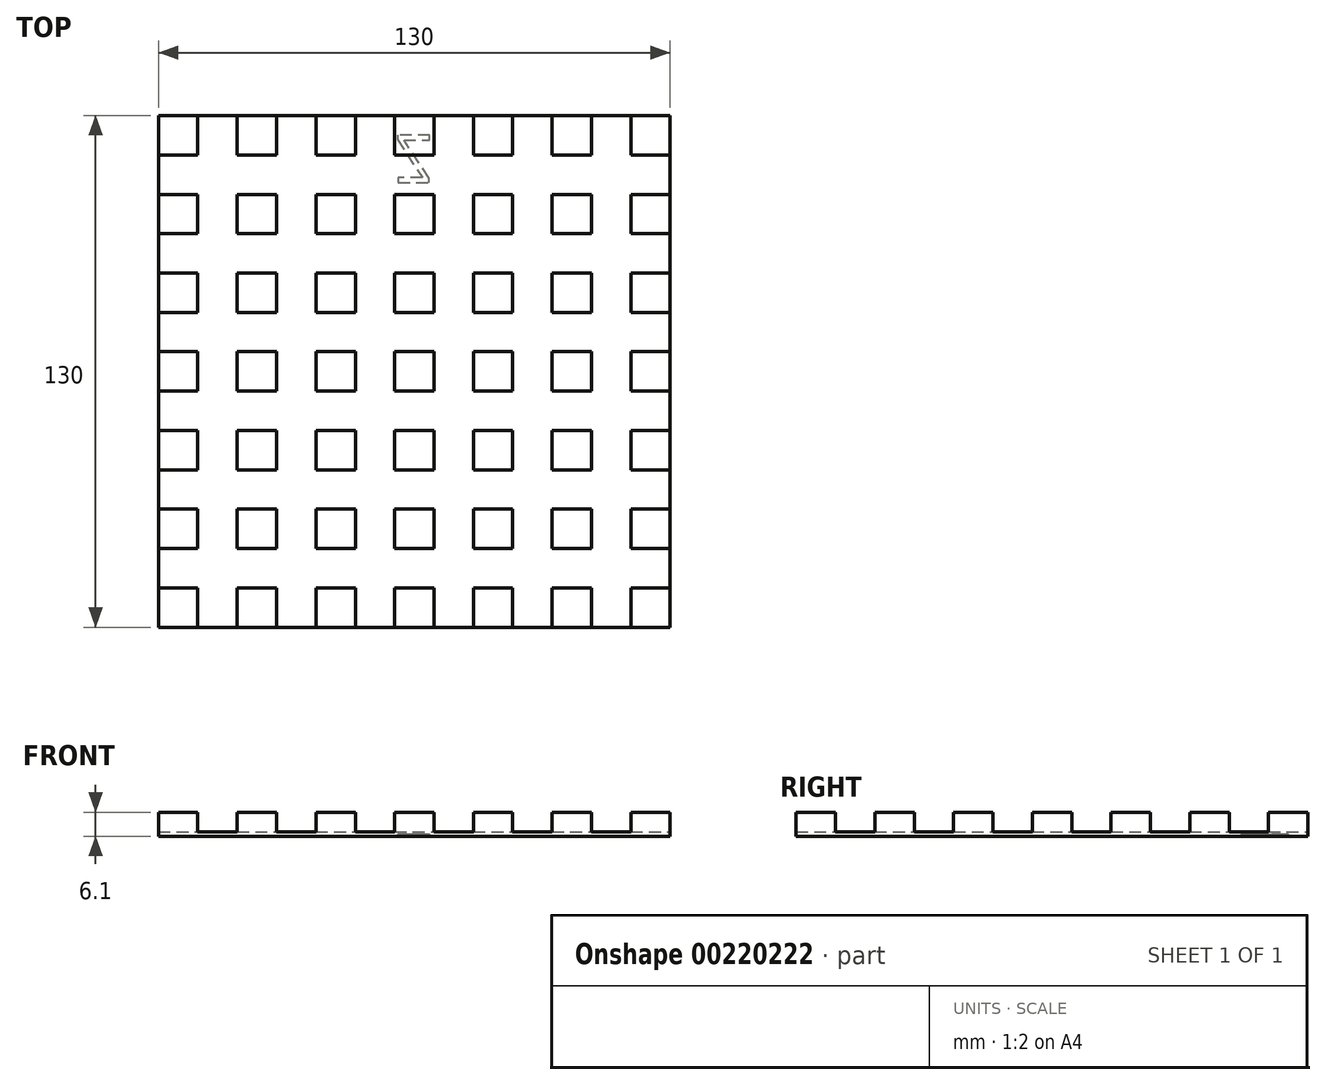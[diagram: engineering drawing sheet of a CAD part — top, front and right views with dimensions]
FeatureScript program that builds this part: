
annotation { "Feature Type Name" : "Feature", "Feature Type Description" : "" }
export const myFeature = defineFeature(function(context is Context, id is Id, definition is map)
    precondition{}
    {
        {
            var Q0;
            Q0=qCreatedBy(makeId("Top.planeOp"),FACE);
            var sketch = newSketch(context, id + "F0", { "sketchPlane" : qUnion([Q0])});
            skLineSegment(sketch, "E0.bottom", {"start": v(0, 0) * mm, "end": v(130, 0) * mm});
            skLineSegment(sketch, "E0.top", {"start": v(0, 130) * mm, "end": v(130, 130) * mm});
            skLineSegment(sketch, "E0.left", {"start": v(0, 0) * mm, "end": v(0, 130) * mm});
            skLineSegment(sketch, "E0.right", {"start": v(130, 0) * mm, "end": v(130, 130) * mm});
            skSolve(sketch);
        }
        {
            var Q0;
            Q0 = qSketchRegion(id + "F0", true);
            extrude(context, id + "F1", {"entities" : qUnion([Q0]), "depth" : 1.1 * mm});
        }
        {
            var Q0;
            Q0=makeQuery(id+"F1.opExtrude","CAP_FACE",FACE,{"disambiguationData":[OSD([sQuery(id+"F0.wireOp",EDGE,"E0.bottom"),sQuery(id+"F0.wireOp",EDGE,"E0.top"),sQuery(id+"F0.wireOp",EDGE,"E0.left"),sQuery(id+"F0.wireOp",EDGE,"E0.right")])],"isStart":false});
            var sketch = newSketch(context, id + "F2", { "sketchPlane" : qUnion([Q0])});
            skLineSegment(sketch, "E1", {"start": v(0, 0) * mm, "end": v(130, 130) * mm, "construction": true});
            skLineSegment(sketch, "E2.bottom", {"start": v(0, 0) * mm, "end": v(130, 0) * mm, "construction": true});
            skLineSegment(sketch, "E2.top", {"start": v(0, 130) * mm, "end": v(130, 130) * mm, "construction": true});
            skLineSegment(sketch, "E2.left", {"start": v(0, 0) * mm, "end": v(0, 130) * mm, "construction": true});
            skLineSegment(sketch, "E2.right", {"start": v(130, 0) * mm, "end": v(130, 130) * mm, "construction": true});
            skPoint(sketch, "E2.middle", {"position": v(65, 65) * mm});
            skLineSegment(sketch, "E3.bottom", {"start": v(0, 0) * mm, "end": v(10, 0) * mm});
            skLineSegment(sketch, "E3.top", {"start": v(0, 10) * mm, "end": v(10, 10) * mm});
            skLineSegment(sketch, "E3.left", {"start": v(0, 0) * mm, "end": v(0, 10) * mm});
            skLineSegment(sketch, "E3.right", {"start": v(10, 0) * mm, "end": v(10, 10) * mm});
            skLineSegment(sketch, "E4.0.1.0", {"start": v(10, 20) * mm, "end": v(10, 30) * mm});
            skLineSegment(sketch, "E4.0.1.1", {"start": v(0, 20) * mm, "end": v(0, 30) * mm});
            skLineSegment(sketch, "E4.0.1.2", {"start": v(0, 20) * mm, "end": v(10, 20) * mm});
            skLineSegment(sketch, "E4.0.1.3", {"start": v(0, 30) * mm, "end": v(10, 30) * mm});
            skLineSegment(sketch, "E4.0.2.0", {"start": v(10, 40) * mm, "end": v(10, 50) * mm});
            skLineSegment(sketch, "E4.0.2.1", {"start": v(0, 40) * mm, "end": v(0, 50) * mm});
            skLineSegment(sketch, "E4.0.2.2", {"start": v(0, 40) * mm, "end": v(10, 40) * mm});
            skLineSegment(sketch, "E4.0.2.3", {"start": v(0, 50) * mm, "end": v(10, 50) * mm});
            skLineSegment(sketch, "E4.0.3.0", {"start": v(10, 60) * mm, "end": v(10, 70) * mm});
            skLineSegment(sketch, "E4.0.3.1", {"start": v(0, 60) * mm, "end": v(0, 70) * mm});
            skLineSegment(sketch, "E4.0.3.2", {"start": v(0, 60) * mm, "end": v(10, 60) * mm});
            skLineSegment(sketch, "E4.0.3.3", {"start": v(0, 70) * mm, "end": v(10, 70) * mm});
            skLineSegment(sketch, "E4.0.4.0", {"start": v(10, 80) * mm, "end": v(10, 90) * mm});
            skLineSegment(sketch, "E4.0.4.1", {"start": v(0, 80) * mm, "end": v(0, 90) * mm});
            skLineSegment(sketch, "E4.0.4.2", {"start": v(0, 80) * mm, "end": v(10, 80) * mm});
            skLineSegment(sketch, "E4.0.4.3", {"start": v(0, 90) * mm, "end": v(10, 90) * mm});
            skLineSegment(sketch, "E4.0.5.0", {"start": v(10, 100) * mm, "end": v(10, 110) * mm});
            skLineSegment(sketch, "E4.0.5.1", {"start": v(0, 100) * mm, "end": v(0, 110) * mm});
            skLineSegment(sketch, "E4.0.5.2", {"start": v(0, 100) * mm, "end": v(10, 100) * mm});
            skLineSegment(sketch, "E4.0.5.3", {"start": v(0, 110) * mm, "end": v(10, 110) * mm});
            skLineSegment(sketch, "E4.1.0.0", {"start": v(30, 0) * mm, "end": v(30, 10) * mm});
            skLineSegment(sketch, "E4.1.0.1", {"start": v(20, 0) * mm, "end": v(20, 10) * mm});
            skLineSegment(sketch, "E4.1.0.2", {"start": v(20, 0) * mm, "end": v(30, 0) * mm});
            skLineSegment(sketch, "E4.1.0.3", {"start": v(20, 10) * mm, "end": v(30, 10) * mm});
            skLineSegment(sketch, "E4.1.1.0", {"start": v(30, 20) * mm, "end": v(30, 30) * mm});
            skLineSegment(sketch, "E4.1.1.1", {"start": v(20, 20) * mm, "end": v(20, 30) * mm});
            skLineSegment(sketch, "E4.1.1.2", {"start": v(20, 20) * mm, "end": v(30, 20) * mm});
            skLineSegment(sketch, "E4.1.1.3", {"start": v(20, 30) * mm, "end": v(30, 30) * mm});
            skLineSegment(sketch, "E4.1.2.0", {"start": v(30, 40) * mm, "end": v(30, 50) * mm});
            skLineSegment(sketch, "E4.1.2.1", {"start": v(20, 40) * mm, "end": v(20, 50) * mm});
            skLineSegment(sketch, "E4.1.2.2", {"start": v(20, 40) * mm, "end": v(30, 40) * mm});
            skLineSegment(sketch, "E4.1.2.3", {"start": v(20, 50) * mm, "end": v(30, 50) * mm});
            skLineSegment(sketch, "E4.1.3.0", {"start": v(30, 60) * mm, "end": v(30, 70) * mm});
            skLineSegment(sketch, "E4.1.3.1", {"start": v(20, 60) * mm, "end": v(20, 70) * mm});
            skLineSegment(sketch, "E4.1.3.2", {"start": v(20, 60) * mm, "end": v(30, 60) * mm});
            skLineSegment(sketch, "E4.1.3.3", {"start": v(20, 70) * mm, "end": v(30, 70) * mm});
            skLineSegment(sketch, "E4.1.4.0", {"start": v(30, 80) * mm, "end": v(30, 90) * mm});
            skLineSegment(sketch, "E4.1.4.1", {"start": v(20, 80) * mm, "end": v(20, 90) * mm});
            skLineSegment(sketch, "E4.1.4.2", {"start": v(20, 80) * mm, "end": v(30, 80) * mm});
            skLineSegment(sketch, "E4.1.4.3", {"start": v(20, 90) * mm, "end": v(30, 90) * mm});
            skLineSegment(sketch, "E4.1.5.0", {"start": v(30, 100) * mm, "end": v(30, 110) * mm});
            skLineSegment(sketch, "E4.1.5.1", {"start": v(20, 100) * mm, "end": v(20, 110) * mm});
            skLineSegment(sketch, "E4.1.5.2", {"start": v(20, 100) * mm, "end": v(30, 100) * mm});
            skLineSegment(sketch, "E4.1.5.3", {"start": v(20, 110) * mm, "end": v(30, 110) * mm});
            skLineSegment(sketch, "E4.2.0.0", {"start": v(50, 0) * mm, "end": v(50, 10) * mm});
            skLineSegment(sketch, "E4.2.0.1", {"start": v(40, 0) * mm, "end": v(40, 10) * mm});
            skLineSegment(sketch, "E4.2.0.2", {"start": v(40, 0) * mm, "end": v(50, 0) * mm});
            skLineSegment(sketch, "E4.2.0.3", {"start": v(40, 10) * mm, "end": v(50, 10) * mm});
            skLineSegment(sketch, "E4.2.1.0", {"start": v(50, 20) * mm, "end": v(50, 30) * mm});
            skLineSegment(sketch, "E4.2.1.1", {"start": v(40, 20) * mm, "end": v(40, 30) * mm});
            skLineSegment(sketch, "E4.2.1.2", {"start": v(40, 20) * mm, "end": v(50, 20) * mm});
            skLineSegment(sketch, "E4.2.1.3", {"start": v(40, 30) * mm, "end": v(50, 30) * mm});
            skLineSegment(sketch, "E4.2.2.0", {"start": v(50, 40) * mm, "end": v(50, 50) * mm});
            skLineSegment(sketch, "E4.2.2.1", {"start": v(40, 40) * mm, "end": v(40, 50) * mm});
            skLineSegment(sketch, "E4.2.2.2", {"start": v(40, 40) * mm, "end": v(50, 40) * mm});
            skLineSegment(sketch, "E4.2.2.3", {"start": v(40, 50) * mm, "end": v(50, 50) * mm});
            skLineSegment(sketch, "E4.2.3.0", {"start": v(50, 60) * mm, "end": v(50, 70) * mm});
            skLineSegment(sketch, "E4.2.3.1", {"start": v(40, 60) * mm, "end": v(40, 70) * mm});
            skLineSegment(sketch, "E4.2.3.2", {"start": v(40, 60) * mm, "end": v(50, 60) * mm});
            skLineSegment(sketch, "E4.2.3.3", {"start": v(40, 70) * mm, "end": v(50, 70) * mm});
            skLineSegment(sketch, "E4.2.4.0", {"start": v(50, 80) * mm, "end": v(50, 90) * mm});
            skLineSegment(sketch, "E4.2.4.1", {"start": v(40, 80) * mm, "end": v(40, 90) * mm});
            skLineSegment(sketch, "E4.2.4.2", {"start": v(40, 80) * mm, "end": v(50, 80) * mm});
            skLineSegment(sketch, "E4.2.4.3", {"start": v(40, 90) * mm, "end": v(50, 90) * mm});
            skLineSegment(sketch, "E4.2.5.0", {"start": v(50, 100) * mm, "end": v(50, 110) * mm});
            skLineSegment(sketch, "E4.2.5.1", {"start": v(40, 100) * mm, "end": v(40, 110) * mm});
            skLineSegment(sketch, "E4.2.5.2", {"start": v(40, 100) * mm, "end": v(50, 100) * mm});
            skLineSegment(sketch, "E4.2.5.3", {"start": v(40, 110) * mm, "end": v(50, 110) * mm});
            skLineSegment(sketch, "E4.3.0.0", {"start": v(70, 0) * mm, "end": v(70, 10) * mm});
            skLineSegment(sketch, "E4.3.0.1", {"start": v(60, 0) * mm, "end": v(60, 10) * mm});
            skLineSegment(sketch, "E4.3.0.2", {"start": v(60, 0) * mm, "end": v(70, 0) * mm});
            skLineSegment(sketch, "E4.3.0.3", {"start": v(60, 10) * mm, "end": v(70, 10) * mm});
            skLineSegment(sketch, "E4.3.1.0", {"start": v(70, 20) * mm, "end": v(70, 30) * mm});
            skLineSegment(sketch, "E4.3.1.1", {"start": v(60, 20) * mm, "end": v(60, 30) * mm});
            skLineSegment(sketch, "E4.3.1.2", {"start": v(60, 20) * mm, "end": v(70, 20) * mm});
            skLineSegment(sketch, "E4.3.1.3", {"start": v(60, 30) * mm, "end": v(70, 30) * mm});
            skLineSegment(sketch, "E4.3.2.0", {"start": v(70, 40) * mm, "end": v(70, 50) * mm});
            skLineSegment(sketch, "E4.3.2.1", {"start": v(60, 40) * mm, "end": v(60, 50) * mm});
            skLineSegment(sketch, "E4.3.2.2", {"start": v(60, 40) * mm, "end": v(70, 40) * mm});
            skLineSegment(sketch, "E4.3.2.3", {"start": v(60, 50) * mm, "end": v(70, 50) * mm});
            skLineSegment(sketch, "E4.3.3.0", {"start": v(70, 60) * mm, "end": v(70, 70) * mm});
            skLineSegment(sketch, "E4.3.3.1", {"start": v(60, 60) * mm, "end": v(60, 70) * mm});
            skLineSegment(sketch, "E4.3.3.2", {"start": v(60, 60) * mm, "end": v(70, 60) * mm});
            skLineSegment(sketch, "E4.3.3.3", {"start": v(60, 70) * mm, "end": v(70, 70) * mm});
            skLineSegment(sketch, "E4.3.4.0", {"start": v(70, 80) * mm, "end": v(70, 90) * mm});
            skLineSegment(sketch, "E4.3.4.1", {"start": v(60, 80) * mm, "end": v(60, 90) * mm});
            skLineSegment(sketch, "E4.3.4.2", {"start": v(60, 80) * mm, "end": v(70, 80) * mm});
            skLineSegment(sketch, "E4.3.4.3", {"start": v(60, 90) * mm, "end": v(70, 90) * mm});
            skLineSegment(sketch, "E4.3.5.0", {"start": v(70, 100) * mm, "end": v(70, 110) * mm});
            skLineSegment(sketch, "E4.3.5.1", {"start": v(60, 100) * mm, "end": v(60, 110) * mm});
            skLineSegment(sketch, "E4.3.5.2", {"start": v(60, 100) * mm, "end": v(70, 100) * mm});
            skLineSegment(sketch, "E4.3.5.3", {"start": v(60, 110) * mm, "end": v(70, 110) * mm});
            skLineSegment(sketch, "E4.4.0.0", {"start": v(90, 0) * mm, "end": v(90, 10) * mm});
            skLineSegment(sketch, "E4.4.0.1", {"start": v(80, 0) * mm, "end": v(80, 10) * mm});
            skLineSegment(sketch, "E4.4.0.2", {"start": v(80, 0) * mm, "end": v(90, 0) * mm});
            skLineSegment(sketch, "E4.4.0.3", {"start": v(80, 10) * mm, "end": v(90, 10) * mm});
            skLineSegment(sketch, "E4.4.1.0", {"start": v(90, 20) * mm, "end": v(90, 30) * mm});
            skLineSegment(sketch, "E4.4.1.1", {"start": v(80, 20) * mm, "end": v(80, 30) * mm});
            skLineSegment(sketch, "E4.4.1.2", {"start": v(80, 20) * mm, "end": v(90, 20) * mm});
            skLineSegment(sketch, "E4.4.1.3", {"start": v(80, 30) * mm, "end": v(90, 30) * mm});
            skLineSegment(sketch, "E4.4.2.0", {"start": v(90, 40) * mm, "end": v(90, 50) * mm});
            skLineSegment(sketch, "E4.4.2.1", {"start": v(80, 40) * mm, "end": v(80, 50) * mm});
            skLineSegment(sketch, "E4.4.2.2", {"start": v(80, 40) * mm, "end": v(90, 40) * mm});
            skLineSegment(sketch, "E4.4.2.3", {"start": v(80, 50) * mm, "end": v(90, 50) * mm});
            skLineSegment(sketch, "E4.4.3.0", {"start": v(90, 60) * mm, "end": v(90, 70) * mm});
            skLineSegment(sketch, "E4.4.3.1", {"start": v(80, 60) * mm, "end": v(80, 70) * mm});
            skLineSegment(sketch, "E4.4.3.2", {"start": v(80, 60) * mm, "end": v(90, 60) * mm});
            skLineSegment(sketch, "E4.4.3.3", {"start": v(80, 70) * mm, "end": v(90, 70) * mm});
            skLineSegment(sketch, "E4.4.4.0", {"start": v(90, 80) * mm, "end": v(90, 90) * mm});
            skLineSegment(sketch, "E4.4.4.1", {"start": v(80, 80) * mm, "end": v(80, 90) * mm});
            skLineSegment(sketch, "E4.4.4.2", {"start": v(80, 80) * mm, "end": v(90, 80) * mm});
            skLineSegment(sketch, "E4.4.4.3", {"start": v(80, 90) * mm, "end": v(90, 90) * mm});
            skLineSegment(sketch, "E4.4.5.0", {"start": v(90, 100) * mm, "end": v(90, 110) * mm});
            skLineSegment(sketch, "E4.4.5.1", {"start": v(80, 100) * mm, "end": v(80, 110) * mm});
            skLineSegment(sketch, "E4.4.5.2", {"start": v(80, 100) * mm, "end": v(90, 100) * mm});
            skLineSegment(sketch, "E4.4.5.3", {"start": v(80, 110) * mm, "end": v(90, 110) * mm});
            skLineSegment(sketch, "E4.5.0.0", {"start": v(110, 0) * mm, "end": v(110, 10) * mm});
            skLineSegment(sketch, "E4.5.0.1", {"start": v(100, 0) * mm, "end": v(100, 10) * mm});
            skLineSegment(sketch, "E4.5.0.2", {"start": v(100, 0) * mm, "end": v(110, 0) * mm});
            skLineSegment(sketch, "E4.5.0.3", {"start": v(100, 10) * mm, "end": v(110, 10) * mm});
            skLineSegment(sketch, "E4.5.1.0", {"start": v(110, 20) * mm, "end": v(110, 30) * mm});
            skLineSegment(sketch, "E4.5.1.1", {"start": v(100, 20) * mm, "end": v(100, 30) * mm});
            skLineSegment(sketch, "E4.5.1.2", {"start": v(100, 20) * mm, "end": v(110, 20) * mm});
            skLineSegment(sketch, "E4.5.1.3", {"start": v(100, 30) * mm, "end": v(110, 30) * mm});
            skLineSegment(sketch, "E4.5.2.0", {"start": v(110, 40) * mm, "end": v(110, 50) * mm});
            skLineSegment(sketch, "E4.5.2.1", {"start": v(100, 40) * mm, "end": v(100, 50) * mm});
            skLineSegment(sketch, "E4.5.2.2", {"start": v(100, 40) * mm, "end": v(110, 40) * mm});
            skLineSegment(sketch, "E4.5.2.3", {"start": v(100, 50) * mm, "end": v(110, 50) * mm});
            skLineSegment(sketch, "E4.5.3.0", {"start": v(110, 60) * mm, "end": v(110, 70) * mm});
            skLineSegment(sketch, "E4.5.3.1", {"start": v(100, 60) * mm, "end": v(100, 70) * mm});
            skLineSegment(sketch, "E4.5.3.2", {"start": v(100, 60) * mm, "end": v(110, 60) * mm});
            skLineSegment(sketch, "E4.5.3.3", {"start": v(100, 70) * mm, "end": v(110, 70) * mm});
            skLineSegment(sketch, "E4.5.4.0", {"start": v(110, 80) * mm, "end": v(110, 90) * mm});
            skLineSegment(sketch, "E4.5.4.1", {"start": v(100, 80) * mm, "end": v(100, 90) * mm});
            skLineSegment(sketch, "E4.5.4.2", {"start": v(100, 80) * mm, "end": v(110, 80) * mm});
            skLineSegment(sketch, "E4.5.4.3", {"start": v(100, 90) * mm, "end": v(110, 90) * mm});
            skLineSegment(sketch, "E4.5.5.0", {"start": v(110, 100) * mm, "end": v(110, 110) * mm});
            skLineSegment(sketch, "E4.5.5.1", {"start": v(100, 100) * mm, "end": v(100, 110) * mm});
            skLineSegment(sketch, "E4.5.5.2", {"start": v(100, 100) * mm, "end": v(110, 100) * mm});
            skLineSegment(sketch, "E4.5.5.3", {"start": v(100, 110) * mm, "end": v(110, 110) * mm});
            skLineSegment(sketch, "E4.direction1", {"start": v(0, 0) * mm, "end": v(20, 0) * mm, "construction": true});
            skLineSegment(sketch, "E4.direction2", {"start": v(0, 0) * mm, "end": v(0, 20) * mm, "construction": true});
            skLineSegment(sketch, "E5.0.0.6", {"start": v(10, 120) * mm, "end": v(10, 130) * mm});
            skLineSegment(sketch, "E5.3.0.6", {"start": v(0, 120) * mm, "end": v(0, 130) * mm});
            skLineSegment(sketch, "E5.6.0.6", {"start": v(0, 120) * mm, "end": v(10, 120) * mm});
            skLineSegment(sketch, "E5.9.0.6", {"start": v(0, 130) * mm, "end": v(10, 130) * mm});
            skLineSegment(sketch, "E5.0.1.6", {"start": v(30, 120) * mm, "end": v(30, 130) * mm});
            skLineSegment(sketch, "E5.3.1.6", {"start": v(20, 120) * mm, "end": v(20, 130) * mm});
            skLineSegment(sketch, "E5.6.1.6", {"start": v(20, 120) * mm, "end": v(30, 120) * mm});
            skLineSegment(sketch, "E5.9.1.6", {"start": v(20, 130) * mm, "end": v(30, 130) * mm});
            skLineSegment(sketch, "E5.0.2.6", {"start": v(50, 120) * mm, "end": v(50, 130) * mm});
            skLineSegment(sketch, "E5.3.2.6", {"start": v(40, 120) * mm, "end": v(40, 130) * mm});
            skLineSegment(sketch, "E5.6.2.6", {"start": v(40, 120) * mm, "end": v(50, 120) * mm});
            skLineSegment(sketch, "E5.9.2.6", {"start": v(40, 130) * mm, "end": v(50, 130) * mm});
            skLineSegment(sketch, "E5.0.3.6", {"start": v(70, 120) * mm, "end": v(70, 130) * mm});
            skLineSegment(sketch, "E5.3.3.6", {"start": v(60, 120) * mm, "end": v(60, 130) * mm});
            skLineSegment(sketch, "E5.6.3.6", {"start": v(60, 120) * mm, "end": v(70, 120) * mm});
            skLineSegment(sketch, "E5.9.3.6", {"start": v(60, 130) * mm, "end": v(70, 130) * mm});
            skLineSegment(sketch, "E5.0.4.6", {"start": v(90, 120) * mm, "end": v(90, 130) * mm});
            skLineSegment(sketch, "E5.3.4.6", {"start": v(80, 120) * mm, "end": v(80, 130) * mm});
            skLineSegment(sketch, "E5.6.4.6", {"start": v(80, 120) * mm, "end": v(90, 120) * mm});
            skLineSegment(sketch, "E5.9.4.6", {"start": v(80, 130) * mm, "end": v(90, 130) * mm});
            skLineSegment(sketch, "E5.0.5.6", {"start": v(110, 120) * mm, "end": v(110, 130) * mm});
            skLineSegment(sketch, "E5.3.5.6", {"start": v(100, 120) * mm, "end": v(100, 130) * mm});
            skLineSegment(sketch, "E5.6.5.6", {"start": v(100, 120) * mm, "end": v(110, 120) * mm});
            skLineSegment(sketch, "E5.9.5.6", {"start": v(100, 130) * mm, "end": v(110, 130) * mm});
            skLineSegment(sketch, "E6.0.6.0", {"start": v(130, 0) * mm, "end": v(130, 10) * mm});
            skLineSegment(sketch, "E6.3.6.0", {"start": v(120, 0) * mm, "end": v(120, 10) * mm});
            skLineSegment(sketch, "E6.6.6.0", {"start": v(120, 0) * mm, "end": v(130, 0) * mm});
            skLineSegment(sketch, "E6.9.6.0", {"start": v(120, 10) * mm, "end": v(130, 10) * mm});
            skLineSegment(sketch, "E6.0.6.1", {"start": v(130, 20) * mm, "end": v(130, 30) * mm});
            skLineSegment(sketch, "E6.3.6.1", {"start": v(120, 20) * mm, "end": v(120, 30) * mm});
            skLineSegment(sketch, "E6.6.6.1", {"start": v(120, 20) * mm, "end": v(130, 20) * mm});
            skLineSegment(sketch, "E6.9.6.1", {"start": v(120, 30) * mm, "end": v(130, 30) * mm});
            skLineSegment(sketch, "E6.0.6.2", {"start": v(130, 40) * mm, "end": v(130, 50) * mm});
            skLineSegment(sketch, "E6.3.6.2", {"start": v(120, 40) * mm, "end": v(120, 50) * mm});
            skLineSegment(sketch, "E6.6.6.2", {"start": v(120, 40) * mm, "end": v(130, 40) * mm});
            skLineSegment(sketch, "E6.9.6.2", {"start": v(120, 50) * mm, "end": v(130, 50) * mm});
            skLineSegment(sketch, "E6.0.6.3", {"start": v(130, 60) * mm, "end": v(130, 70) * mm});
            skLineSegment(sketch, "E6.3.6.3", {"start": v(120, 60) * mm, "end": v(120, 70) * mm});
            skLineSegment(sketch, "E6.6.6.3", {"start": v(120, 60) * mm, "end": v(130, 60) * mm});
            skLineSegment(sketch, "E6.9.6.3", {"start": v(120, 70) * mm, "end": v(130, 70) * mm});
            skLineSegment(sketch, "E6.0.6.4", {"start": v(130, 80) * mm, "end": v(130, 90) * mm});
            skLineSegment(sketch, "E6.3.6.4", {"start": v(120, 80) * mm, "end": v(120, 90) * mm});
            skLineSegment(sketch, "E6.6.6.4", {"start": v(120, 80) * mm, "end": v(130, 80) * mm});
            skLineSegment(sketch, "E6.9.6.4", {"start": v(120, 90) * mm, "end": v(130, 90) * mm});
            skLineSegment(sketch, "E6.0.6.5", {"start": v(130, 100) * mm, "end": v(130, 110) * mm});
            skLineSegment(sketch, "E6.3.6.5", {"start": v(120, 100) * mm, "end": v(120, 110) * mm});
            skLineSegment(sketch, "E6.6.6.5", {"start": v(120, 100) * mm, "end": v(130, 100) * mm});
            skLineSegment(sketch, "E6.9.6.5", {"start": v(120, 110) * mm, "end": v(130, 110) * mm});
            skLineSegment(sketch, "E6.0.6.6", {"start": v(130, 120) * mm, "end": v(130, 130) * mm});
            skLineSegment(sketch, "E6.3.6.6", {"start": v(120, 120) * mm, "end": v(120, 130) * mm});
            skLineSegment(sketch, "E6.6.6.6", {"start": v(120, 120) * mm, "end": v(130, 120) * mm});
            skLineSegment(sketch, "E6.9.6.6", {"start": v(120, 130) * mm, "end": v(130, 130) * mm});
            skSolve(sketch);
        }
        {
            var Q0;
            Q0 = qSketchRegion(id + "F2", true);
            extrude(context, id + "F3", {"entities" : qUnion([Q0]), "operationType" : NewBodyOperationType.ADD, "depth" : 5 * mm});
        }
        {
            var Q0;
            Q0=makeQuery(id+"F1.opExtrude","CAP_FACE",FACE,{"disambiguationData":[OSD([sQuery(id+"F0.wireOp",EDGE,"E0.bottom"),sQuery(id+"F0.wireOp",EDGE,"E0.top"),sQuery(id+"F0.wireOp",EDGE,"E0.left"),sQuery(id+"F0.wireOp",EDGE,"E0.right")])],"isStart":true});
            var sketch = newSketch(context, id + "F4", { "sketchPlane" : qUnion([Q0])});
            skText(sketch, "E7", { "text": "Z", "fontName": "OpenSans-Regular.ttf"});
            skLineSegment(sketch, "E8", {"start": v(65, -125) * mm, "end": v(65, -130) * mm, "construction": true});
            const initialGuessF4  = {"E7": [0.06, -0.125, 1, 0, 0.01209]};
            skSetInitialGuess(sketch, initialGuessF4);
            skSolve(sketch);
        }
        {
            var Q0;
            Q0 = qSketchRegion(id + "F4", true);
            extrude(context, id + "F5", {"entities" : qUnion([Q0]), "operationType" : NewBodyOperationType.REMOVE, "oppositeDirection" : true, "depth" : 0.5 * mm});
        }
    });
